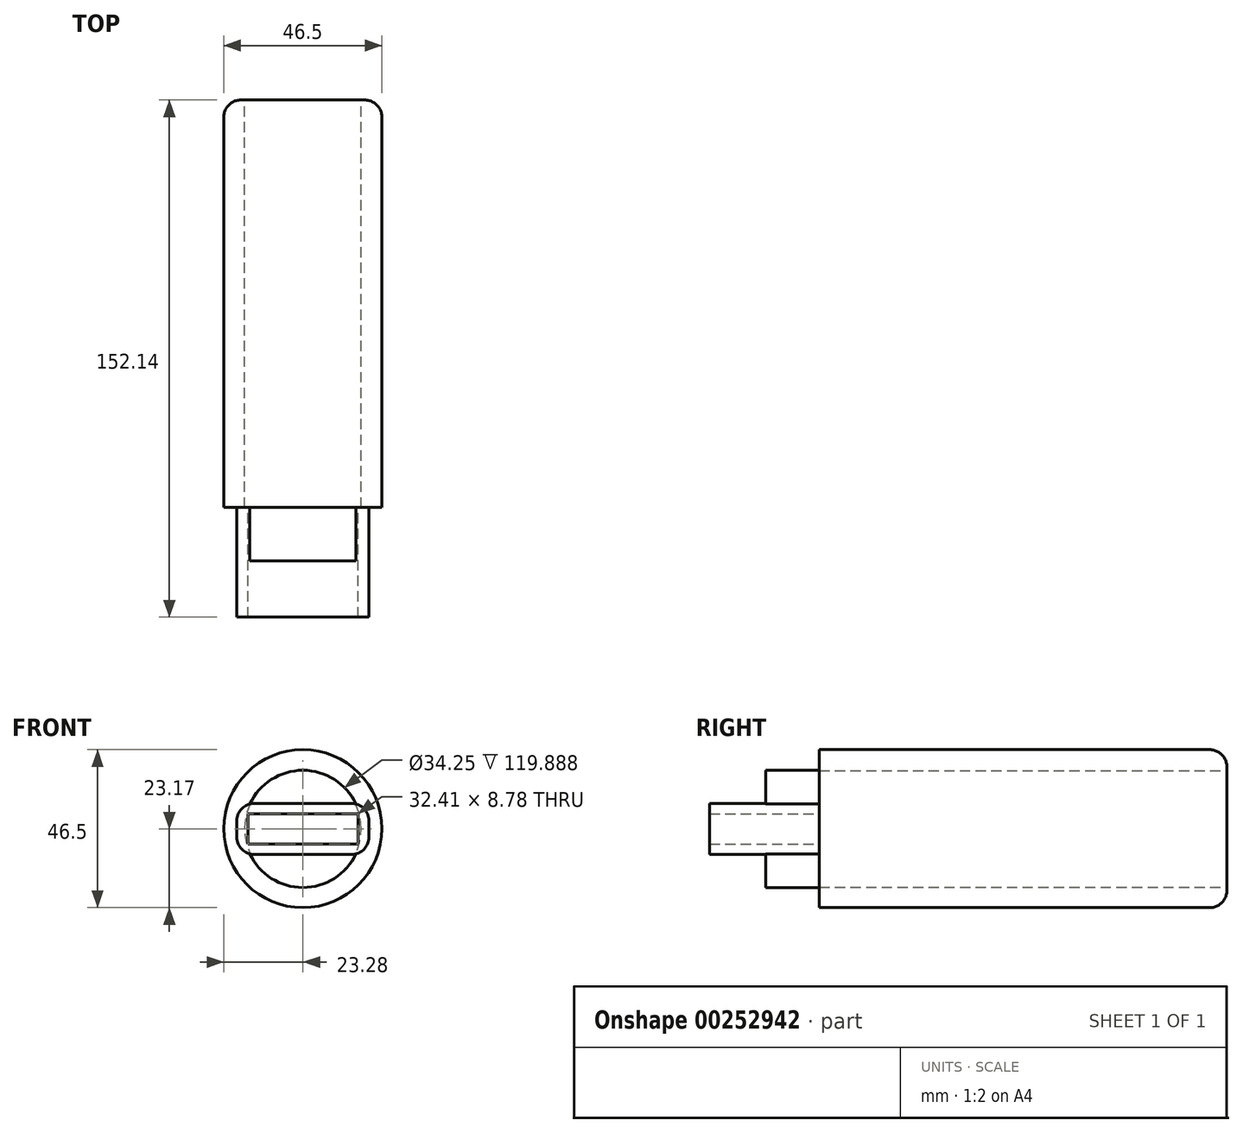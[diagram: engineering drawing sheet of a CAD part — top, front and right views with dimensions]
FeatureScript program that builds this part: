
annotation { "Feature Type Name" : "Feature", "Feature Type Description" : "" }
export const myFeature = defineFeature(function(context is Context, id is Id, definition is map)
    precondition{}
    {
        {
            var Q0;
            Q0=qCreatedBy(makeId("Front.planeOp"),FACE);
            var sketch = newSketch(context, id + "F0", { "sketchPlane" : qUnion([Q0])});
            skCircle(sketch, "E0", {"center": v(0, 0) * mm, "radius": 17.13 * mm});
            skCircle(sketch, "E1", {"center": v(-0.03, 0.08) * mm, "radius": 23.25 * mm});
            skSolve(sketch);
        }
        {
            var Q0;
            Q0=makeQuery(id+"F0.imprint","IMPRINT",FACE,{"disambiguationData":[TD([[makeQuery(id+"F0.imprint","IMPRINT",EDGE,{"derivedFrom":sQuery(id+"F0.wireOp",EDGE,"E0")}),-1.0]])]});
            extrude(context, id + "F1", {"entities" : qUnion([Q0]), "endBound" : BoundingType.SYMMETRIC, "depth" : 119.89 * mm});
        }
        {
            var Q0;
            Q0=makeQuery(id+"F1.opExtrude","CAP_EDGE",EDGE,{"disambiguationData":[OSD([sQuery(id+"F0.wireOp",EDGE,"E1")])],"isStart":true});
            fillet(context, id + "F2", {"entities" : qUnion([Q0]), "radius" : 5.08 * mm, "tangentPropagation" : true, "allowEdgeOverflow" : false});
        }
        {
            var Q0;
            Q0=makeQuery(id+"F1.opExtrude","CAP_FACE",FACE,{"disambiguationData":[OSD([sQuery(id+"F0.wireOp",EDGE,"E0"),sQuery(id+"F0.wireOp",EDGE,"E1")])],"isStart":false});
            var sketch = newSketch(context, id + "F3", { "sketchPlane" : qUnion([Q0])});
            skSolve(sketch);
        }
        {
            var Q0;
            Q0=makeQuery(id+"F3.imprint","IMPRINT",FACE,{"disambiguationData":[TD([[makeQuery(id+"F3.imprint","IMPRINT",EDGE,{"derivedFrom":makeQuery(id+"F1.opExtrude","CAP_EDGE",EDGE,{"disambiguationData":[OSD([sQuery(id+"F0.wireOp",EDGE,"E0")])],"isStart":false})}),-1.0]])]});
            var sketch = newSketch(context, id + "F4", { "sketchPlane" : qUnion([Q0])});
            skLineSegment(sketch, "E2.bottom", {"start": v(-19.44, 7.48) * mm, "end": v(19.44, 7.48) * mm});
            skLineSegment(sketch, "E2.top", {"start": v(-19.44, -7.48) * mm, "end": v(19.44, -7.48) * mm});
            skLineSegment(sketch, "E2.left", {"start": v(-19.44, 7.48) * mm, "end": v(-19.44, -7.48) * mm});
            skLineSegment(sketch, "E2.right", {"start": v(19.44, 7.48) * mm, "end": v(19.44, -7.48) * mm});
            skPoint(sketch, "E2.middle", {"position": v(0, 0) * mm});
            skLineSegment(sketch, "E3.bottom", {"start": v(-16.2, 4.4) * mm, "end": v(16.2, 4.4) * mm});
            skLineSegment(sketch, "E3.top", {"start": v(-16.2, -4.4) * mm, "end": v(16.2, -4.4) * mm});
            skLineSegment(sketch, "E3.left", {"start": v(-16.2, 4.4) * mm, "end": v(-16.2, -4.4) * mm});
            skLineSegment(sketch, "E3.right", {"start": v(16.2, 4.4) * mm, "end": v(16.2, -4.4) * mm});
            skArc(sketch, "E4.trimOffspring", {"start": v(15.54, 7.48) * mm, "mid": v(0, 17.24) * mm, "end": v(-15.54, 7.48) * mm});
            skLineSegment(sketch, "E5", {"start": v(0, 0) * mm, "end": v(24.67, 0) * mm, "construction": true});
            skArc(sketch, "E6.MirrorCS", {"start": v(15.54, -7.48) * mm, "mid": v(0, -17.24) * mm, "end": v(-15.54, -7.48) * mm});
            skSolve(sketch);
        }
        {
            var Q0;
            Q0 = qSketchRegion(id + "F4", true);
            extrude(context, id + "F5", {"entities" : qUnion([Q0]), "operationType" : NewBodyOperationType.ADD, "depth" : 32.26 * mm});
        }
        {
            var Q0;
            Q0=makeQuery(id+"F5.opExtrude","CAP_FACE",FACE,{"disambiguationData":[OSD([sQuery(id+"F4.wireOp",EDGE,"E2.bottom"),sQuery(id+"F4.wireOp",EDGE,"E2.top"),sQuery(id+"F4.wireOp",EDGE,"E2.left"),sQuery(id+"F4.wireOp",EDGE,"E2.right"),sQuery(id+"F4.wireOp",EDGE,"E3.bottom"),sQuery(id+"F4.wireOp",EDGE,"E3.top"),sQuery(id+"F4.wireOp",EDGE,"E3.left"),sQuery(id+"F4.wireOp",EDGE,"E3.right"),sQuery(id+"F4.wireOp",EDGE,"E4.trimOffspring"),sQuery(id+"F4.wireOp",EDGE,"E6.MirrorCS")])],"isStart":false});
            var sketch = newSketch(context, id + "F6", { "sketchPlane" : qUnion([Q0])});
            skLineSegment(sketch, "E7.bottom", {"start": v(-15.54, 7.48) * mm, "end": v(16.23, 7.48) * mm});
            skLineSegment(sketch, "E7.top", {"start": v(-15.54, 18.82) * mm, "end": v(16.23, 18.82) * mm});
            skLineSegment(sketch, "E7.left", {"start": v(-15.54, 7.48) * mm, "end": v(-15.54, 18.82) * mm});
            skLineSegment(sketch, "E7.right", {"start": v(16.23, 7.48) * mm, "end": v(16.23, 18.82) * mm});
            skLineSegment(sketch, "E8.bottom", {"start": v(15.54, -7.48) * mm, "end": v(-15.54, -7.48) * mm});
            skLineSegment(sketch, "E8.top", {"start": v(15.54, -22.36) * mm, "end": v(-15.54, -22.36) * mm});
            skLineSegment(sketch, "E8.left", {"start": v(15.54, -7.48) * mm, "end": v(15.54, -22.36) * mm});
            skLineSegment(sketch, "E8.right", {"start": v(-15.54, -7.48) * mm, "end": v(-15.54, -22.36) * mm});
            skSolve(sketch);
        }
        {
            var Q0;
            Q0 = qSketchRegion(id + "F6", true);
            extrude(context, id + "F7", {"entities" : qUnion([Q0]), "operationType" : NewBodyOperationType.REMOVE, "oppositeDirection" : true, "depth" : 16.5 * mm});
        }
        {
            var Q0;
            Q0=makeQuery(id+"F5.opExtrude","SWEPT_EDGE",EDGE,{"disambiguationData":[OSD([sQuery(id+"F4.wireOp",EDGE,"E2.top"),sQuery(id+"F4.wireOp",EDGE,"E2.left")])]});
            var Q1;
            Q1=makeQuery(id+"F5.opExtrude","SWEPT_EDGE",EDGE,{"disambiguationData":[OSD([sQuery(id+"F4.wireOp",EDGE,"E2.top"),sQuery(id+"F4.wireOp",EDGE,"E2.right")])]});
            var Q2;
            Q2=makeQuery(id+"F5.opExtrude","SWEPT_EDGE",EDGE,{"disambiguationData":[OSD([sQuery(id+"F4.wireOp",EDGE,"E2.bottom"),sQuery(id+"F4.wireOp",EDGE,"E2.right")])]});
            var Q3;
            Q3=makeQuery(id+"F5.opExtrude","SWEPT_EDGE",EDGE,{"disambiguationData":[OSD([sQuery(id+"F4.wireOp",EDGE,"E2.bottom"),sQuery(id+"F4.wireOp",EDGE,"E2.left")])]});
            fillet(context, id + "F8", {"entities" : qUnion([Q0, Q1, Q2, Q3]), "radius" : 5.08 * mm, "tangentPropagation" : true, "allowEdgeOverflow" : false});
        }
    });
